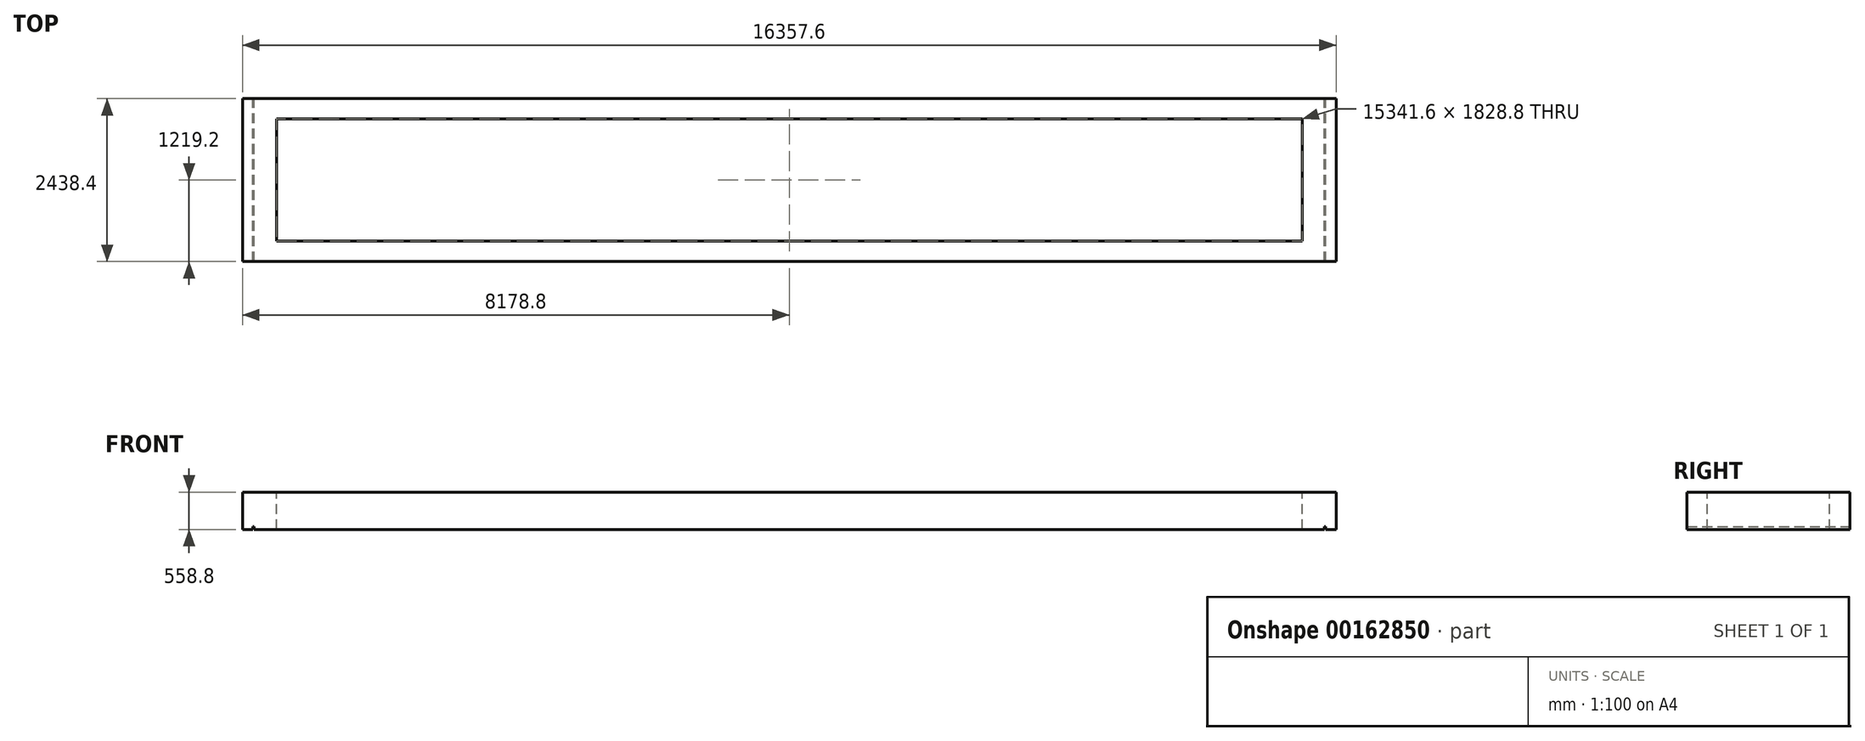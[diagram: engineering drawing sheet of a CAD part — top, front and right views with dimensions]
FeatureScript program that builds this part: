
annotation { "Feature Type Name" : "Feature", "Feature Type Description" : "" }
export const myFeature = defineFeature(function(context is Context, id is Id, definition is map)
    precondition{}
    {
        {
            var Q0;
            Q0=qCreatedBy(makeId("Front.planeOp"),FACE);
            var sketch = newSketch(context, id + "F0", { "sketchPlane" : qUnion([Q0])});
            skLineSegment(sketch, "E0.bottom", {"start": v(8178.8, -279.4) * mm, "end": v(8023.23, -279.4) * mm});
            skLineSegment(sketch, "E0.top", {"start": v(8178.8, 279.4) * mm, "end": v(-8178.8, 279.4) * mm});
            skLineSegment(sketch, "E0.left", {"start": v(8178.8, -279.4) * mm, "end": v(8178.8, 279.4) * mm});
            skLineSegment(sketch, "E0.right", {"start": v(-8178.8, -279.4) * mm, "end": v(-8178.8, 279.4) * mm});
            skPoint(sketch, "E0.middle", {"position": v(0, 0) * mm});
            skLineSegment(sketch, "E1.top", {"start": v(-8023.23, -240.03) * mm, "end": v(-8004.18, -240.03) * mm});
            skLineSegment(sketch, "E1.left", {"start": v(-8023.23, -279.4) * mm, "end": v(-8023.23, -240.03) * mm});
            skLineSegment(sketch, "E1.right", {"start": v(-8004.18, -279.4) * mm, "end": v(-8004.18, -240.03) * mm});
            skLineSegment(sketch, "E2.MirrorCS", {"start": v(8023.23, -240.03) * mm, "end": v(8004.18, -240.03) * mm});
            skLineSegment(sketch, "E3.MirrorCS", {"start": v(8023.23, -279.4) * mm, "end": v(8023.23, -240.03) * mm});
            skLineSegment(sketch, "E4.MirrorCS", {"start": v(8004.18, -279.4) * mm, "end": v(8004.18, -240.03) * mm});
            skLineSegment(sketch, "E5.trimOffspring", {"start": v(8004.18, -279.4) * mm, "end": v(-8004.18, -279.4) * mm});
            skLineSegment(sketch, "E6.trimOffspring", {"start": v(-8023.23, -279.4) * mm, "end": v(-8178.8, -279.4) * mm});
            skSolve(sketch);
        }
        {
            var Q0;
            Q0 = qSketchRegion(id + "F0", true);
            extrude(context, id + "F1", {"entities" : qUnion([Q0]), "depth" : 2438.4 * mm});
        }
        {
            var Q0;
            Q0=makeQuery(id+"F1.opExtrude","SWEPT_FACE",FACE,{"disambiguationData":[OSD([sQuery(id+"F0.wireOp",EDGE,"E0.top")])]});
            var sketch = newSketch(context, id + "F2", { "sketchPlane" : qUnion([Q0])});
            skLineSegment(sketch, "E7.bottom", {"start": v(7670.8, -2133.6) * mm, "end": v(-7670.8, -2133.6) * mm});
            skLineSegment(sketch, "E7.top", {"start": v(7670.8, -304.8) * mm, "end": v(-7670.8, -304.8) * mm});
            skPoint(sketch, "E7.middle", {"position": v(0, -1219.2) * mm});
            skPoint(sketch, "E7.middle.positionSnap0", {"position": v(-8178.8, -1219.2) * mm});
            skPoint(sketch, "E7.middle.positionSnap1", {"position": v(0, -2438.4) * mm});
            skPoint(sketch, "E7.centerSnap0", {"position": v(-8178.8, -1219.2) * mm});
            skPoint(sketch, "E7.centerSnap1", {"position": v(0, -2438.4) * mm});
            skLineSegment(sketch, "E8", {"start": v(7670.8, -304.8) * mm, "end": v(7670.8, -2133.6) * mm});
            skPoint(sketch, "E7.left.end.orphan", {"position": v(10581.12, -304.8) * mm});
            skPoint(sketch, "E9.orphan", {"position": v(10581.12, -2133.6) * mm});
            skLineSegment(sketch, "E10", {"start": v(-7670.8, -304.8) * mm, "end": v(-7670.8, -2133.6) * mm});
            skPoint(sketch, "E7.right.end.orphan", {"position": v(-10581.12, -304.8) * mm});
            skPoint(sketch, "E11.orphan", {"position": v(-10581.12, -2133.6) * mm});
            skSolve(sketch);
        }
        {
            var Q0;
            Q0 = qSketchRegion(id + "F2", true);
            extrude(context, id + "F3", {"entities" : qUnion([Q0]), "operationType" : NewBodyOperationType.REMOVE, "endBound" : BoundingType.THROUGH_ALL, "oppositeDirection" : true, "depth" : 25.4 * mm});
        }
    });
